# Revit family: Flexible Couplings-Zurn_Wilkins-FP23F (114-8_inch)
name_source: partatom
category: Pipe Accessories
units: mm (PartAtom-declared; Revit-internal decimal feet)

## family parameters
Always vertical = Yes
Cut with Voids When Loaded = No
OmniClass Number = 23.65.55.14.11
OmniClass Title = Inlet/Outlet Valves for Liquid Services
Part Type = Valve - Breaks Into
Round Connector Dimension = Use Radius
Shared = No
Work Plane-Based = No

## types (8) — shared parameters
Assembly Code = D2020300
Default Elevation = 0' - 0"
Description = FLEXIBLE FIRE COUPLINGS
Flow Rate (GPM) = 0 GPM
Height = 1' - 0"
Hydrostatic Test Pressure = 0.00 psi
Length = 2' - 0"
Main Material = Paint - Zurn - Ductile Iron Red
Manufacturer = Zurn Water, LLC
Manufacturer Brand = Zurn Wilkins
Max Working Water Pressure = 300.00 psi
Max Working Water Temperature = 0 °F
Modified Date = 10/09/25
Product Documentation Link = https://files.zurn.com
Product Installation Sheet URL = https://files.zurn.com
Product Page URL = https://www.zurn.com
Product data URL = https://www.bimobject.com
URL = https://www.zurn.com
Width = 1' - 0"

## per-type parameters (varying)
| type | Center to end | D | DIM A | DIM B | DIM C | E | F | FP23F-SYMBOL | G | H | I | J | K | L | Model | Nominal Diameter | Nominal Radius | Product Weight (lbs) |
| 3‐FP23F (3" FP23F) | 0' - 3 1/4" | 0' - 1 1/2" | 0' - 6 1/2" | 0' - 4 9/16" | 0' - 1 25/32" | 0' - 3 1/2" | 0' - 0 3/4" | Flexible couplings-Zurn_Wilkins-FP23F_Symbol : 3‐FP23F | 0' - 1 3/32" | 0' - 0 13/32" | 0' - 0 3/4" | 0' - 0 9/32" | 0' - 0 1/4" | 0' - 0 3/16" | 3‐FP23F | 0' - 3" | 0' - 1 1/2" | 2 |
| 114‐FP23F (1 1/4" FP23F) | 0' - 2 3/32" | 0' - 0 11/16" | 0' - 4 7/32" | 0' - 2 21/32" | 0' - 1 23/32" | 0' - 2" | 0' - 0 19/32" | Flexible couplings-Zurn_Wilkins-FP23F_Symbol : 114‐FP23F | 0' - 0 13/32" | 0' - 0 11/32" | 0' - 0 1/2" | 0' - 0 3/16" | 0' - 0 3/16" | 0' - 0 5/32" | 114‐FP23F | 0' - 1 1/4" | 0' - 0 5/8" | 1 |
| 112‐FP23F (1 1/2" FP23F) | 0' - 2 3/16" | 0' - 0 13/16" | 0' - 4 3/8" | 0' - 2 27/32" | 0' - 1 23/32" | 0' - 2 3/16" | 0' - 0 19/32" | Flexible couplings-Zurn_Wilkins-FP23F_Symbol : 112‐FP23F | 0' - 0 1/2" | 0' - 0 11/32" | 0' - 0 19/32" | 0' - 0 3/16" | 0' - 0 1/4" | 0' - 0 1/8" | 112‐FP23F | 0' - 1 1/2" | 0' - 0 3/4" | 1 |
| 2‐FP23F (2" FP23F) | 0' - 2 7/16" | 0' - 1" | 0' - 4 7/8" | 0' - 3 11/32" | 0' - 1 23/32" | 0' - 2 1/2" | 0' - 0 19/32" | Flexible couplings-Zurn_Wilkins-FP23F_Symbol : 2‐FP23F | 0' - 0 19/32" | 0' - 0 11/32" | 0' - 0 19/32" | 0' - 0 3/16" | 0' - 0 1/4" | 0' - 0 1/8" | 2‐FP23F | 0' - 2" | 0' - 1" | 2 |
| 212‐FP23F (2 1/2" FP23F) | 0' - 2 23/32" | 0' - 1 5/16" | 0' - 5 7/16" | 0' - 3 29/32" | 0' - 1 25/32" | 0' - 3" | 0' - 0 19/32" | Flexible couplings-Zurn_Wilkins-FP23F_Symbol : 212‐FP23F | 0' - 0 29/32" | 0' - 0 11/32" | 0' - 0 19/32" | 0' - 0 3/16" | 0' - 0 1/4" | 0' - 0 1/8" | 212‐FP23F | 0' - 2 1/2" | 0' - 1 1/4" | 2 |
| 4‐FP23F (4" FP23F) | 0' - 3 3/4" | 0' - 2" | 0' - 7 15/32" | 0' - 5 9/16" | 0' - 1 15/16" | 0' - 4 3/16" | 0' - 0 13/16" | Flexible couplings-Zurn_Wilkins-FP23F_Symbol : 4‐FP23F | 0' - 1 1/2" | 0' - 0 7/16" | 0' - 0 3/4" | 0' - 0 9/32" | 0' - 0 1/4" | 0' - 0 3/16" | 4‐FP23F | 0' - 4" | 0' - 2" | 3 |
| 6‐FP23F (6" FP23F) | 0' - 4 29/32" | 0' - 3" | 0' - 9 27/32" | 0' - 7 7/8" | 0' - 1 15/16" | 0' - 6" | 0' - 0 29/32" | Flexible couplings-Zurn_Wilkins-FP23F_Symbol : 6‐FP23F | 0' - 2 1/2" | 0' - 0 1/2" | 0' - 0 29/32" | 0' - 0 13/32" | 0' - 0 5/16" | 0' - 0 3/16" | 6‐FP23F | 0' - 6" | 0' - 3" | 5 |
| 8‐FP23F (8" FP23F) | 0' - 6 9/32" | 0' - 4" | 1' - 0 9/16" | 0' - 9 31/32" | 0' - 2 5/16" | 0' - 8" | 0' - 1 3/16" | Flexible couplings-Zurn_Wilkins-FP23F_Symbol : 8‐FP23F | 0' - 3 1/2" | 0' - 0 11/16" | 0' - 1 3/32" | 0' - 0 7/16" | 0' - 0 13/32" | 0' - 0 3/16" | 8‐FP23F | 0' - 8" | 0' - 4" | 8 |

## geometry (parser evidence)
native form markers: Sweep x3
no freeform markers — native parametric forms only
